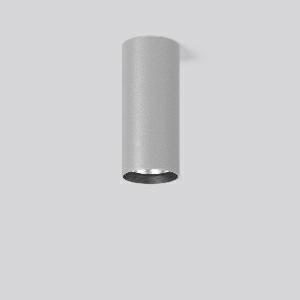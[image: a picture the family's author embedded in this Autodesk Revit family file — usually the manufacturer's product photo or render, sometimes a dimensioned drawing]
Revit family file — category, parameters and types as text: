
# Revit family: heledon_mini_a_931201_004_1_76_0c5a
name_source: partatom
category: Lighting Fixtures
units: mm (PartAtom-declared; Revit-internal decimal feet)

## family parameters
Cut with Voids When Loaded = No
Host = Face
Light Source = No
Part Type = Normal
Room Calculation Point = No
Round Connector Dimension = Use Diameter
Shared = No

## types (1)
- HELEDON mini A (1 x LED Modul 940, 2600 lm, 4000)
    Apparent Load = 20 VA
    Approval mark = CE
    CIE Flux Codes = 99 100 100 100 100
    Color Rendering = 92
    Color Temperature = 4000
    Default Elevation = 1800 mm
    Description = Series: HELEDON mini
Cylindrical surface-mounted downlight. Housing: die-cast aluminium, powder-coated. Internal ceiling frame polycarbonate with bayonet mounting. Black plastic ring and recessed LED to prevent glare from the side. Optical assembly with reflector made of MIRO-Silver with 98% total light reflection for outstanding efficiency - can be changed without tools. Best colour rendering index Ra>90. Suitable for Ceiling mounting. Easy installation with a separate ceiling frame with bayonet mounting and plug connection. Driver integrated. Connected via plug-in connector. High quality converter without flickering and stroboscopic effect. The following accessories can be mounted without use of tools: interchangeable lenses, decorative glasses, honeycomb louvre, clear and frosted diffusers, white interchangeable plastic ring. 
Colour: silver
Diameter: 87 mm
Height: 197 mm
Lamp: LED
Socket: without socket
Colour temperature: 4000K
Colour rendering index (CRI): 92
System power: 20 W
Rated luminous flux: 2600 lm
Luminous efficiency: 130 lm/W
Control gear: Converter, dimmable, DALI
Protection class: I
Type of protection: IP 20
    Height = 197 mm
    Lamp = 1 x LED Modul 940
    Lamp Light Flux = 2600 lm
    Lamp count = 1
    Length = 87 mm
    Lifetime = 50000 h
    Luminous efficacy = 130 lm/W
    Manufacturer = RZB
    ModVariant = No
    Model = 931201.004.1.76
    Mounting Place = Ceiling
    Mounting Type = Surface mounted
    Number of Poles = 1
    OnlyDefault = Yes
    Power Factor = 1
    Product Name = HELEDON mini A
    Product group = Surface mounted downlights
    ProductGroupID = 302
    Protection Class = Protection class I
    Protection Degree = IP 20
    RLX_Detail_Level = 1
    RLX_Emergency_Light_Flux = 0 lm
    RLX_Emergency_Type = 0
    RLX_Emergency_Type_DB = No
    RlxData = <blob elided: 109025 chars, md5=d1f2843a>
    Socket = socket
    Standby Power = 0 W
    System Light Flux = 2600 lm
    System Power = 20 W
    Type Comments = Product without accessories
    Type Image = 931188.004.jpg
    URL = http://relux.com
    VarID = ---
    Voltage = 230 V
    Voltage Range = 220-240 V
    Weight = 0.00 kg
    Width = 0 mm  [stored 0 ft]

note: [stored X ft] marks values corroborated as IEEE doubles in the binary element streams (Revit-internal decimal feet)

## geometry (parser evidence)
native form markers: Blend x4, Sweep x10
no freeform markers — native parametric forms only
